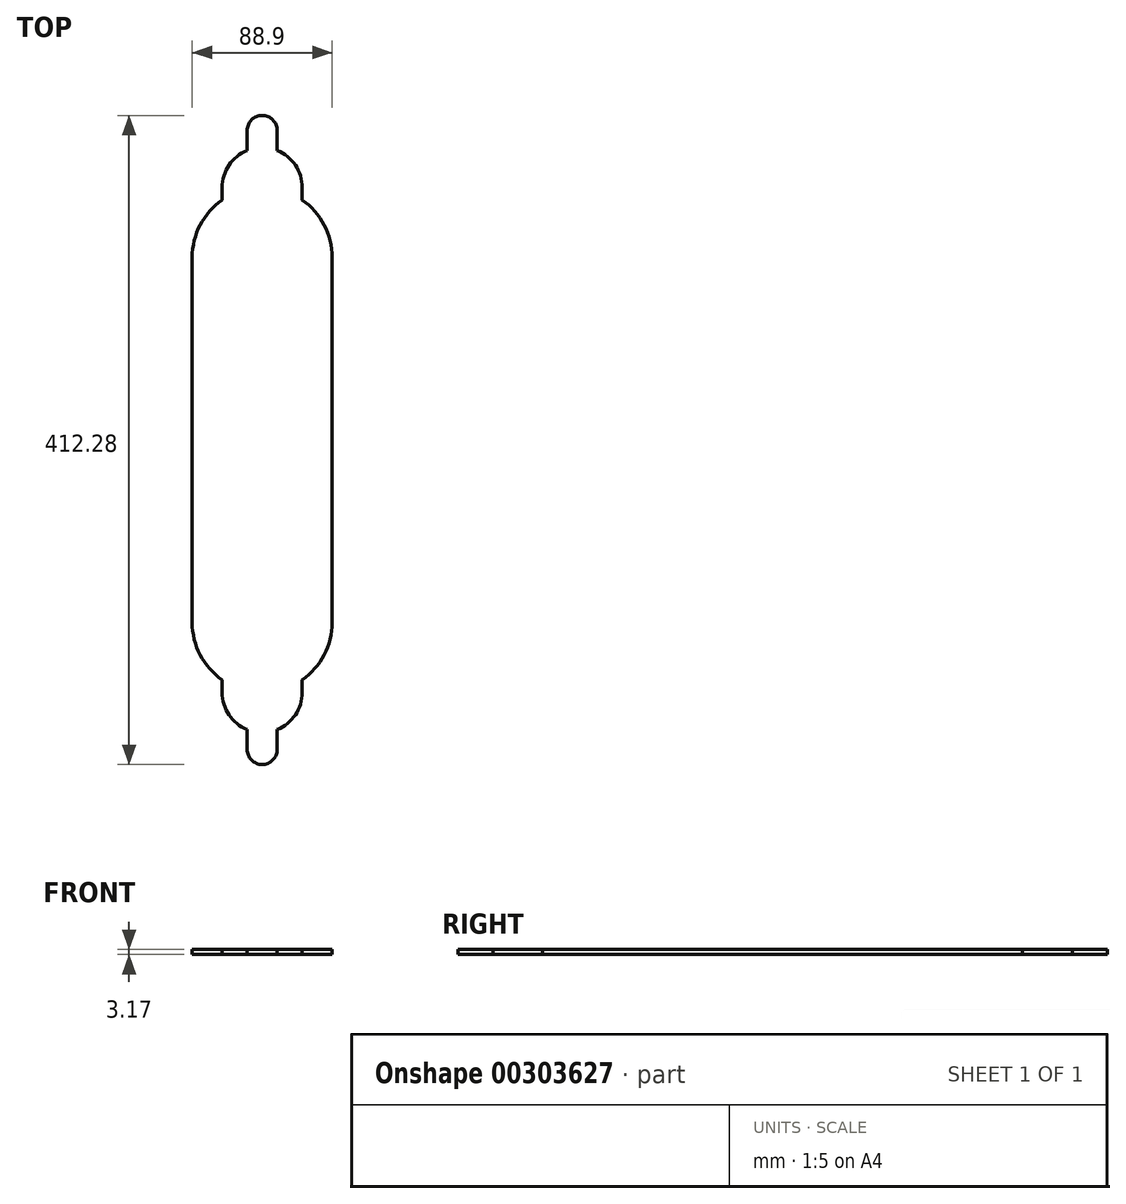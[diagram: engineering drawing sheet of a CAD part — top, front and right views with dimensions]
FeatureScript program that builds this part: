
annotation { "Feature Type Name" : "Feature", "Feature Type Description" : "" }
export const myFeature = defineFeature(function(context is Context, id is Id, definition is map)
    precondition{}
    {
        {
            var Q0;
            Q0=qCreatedBy(makeId("Top.planeOp"),FACE);
            var sketch = newSketch(context, id + "F0", { "sketchPlane" : qUnion([Q0])});
            skLineSegment(sketch, "E0.top", {"start": v(0, 263.5) * mm, "end": v(88.9, 263.5) * mm, "construction": true});
            skLineSegment(sketch, "E0.left", {"start": v(0, 147.59) * mm, "end": v(0, 263.5) * mm});
            skLineSegment(sketch, "E0.right", {"start": v(88.9, 147.59) * mm, "end": v(88.9, 263.5) * mm});
            skArc(sketch, "E1", {"start": v(69.85, 111.1) * mm, "mid": v(83.85, 127.01) * mm, "end": v(88.9, 147.59) * mm});
            skArc(sketch, "E2", {"start": v(53.98, 79.6) * mm, "mid": v(65.51, 88.94) * mm, "end": v(69.85, 103.14) * mm});
            skLineSegment(sketch, "E3", {"start": v(44.45, 147.59) * mm, "end": v(44.45, 66.9) * mm, "construction": true});
            skArc(sketch, "E4", {"start": v(34.93, 66.9) * mm, "mid": v(44.45, 57.37) * mm, "end": v(53.98, 66.9) * mm});
            skLineSegment(sketch, "E5", {"start": v(34.93, 66.9) * mm, "end": v(34.93, 79.6) * mm});
            skLineSegment(sketch, "E6", {"start": v(53.98, 66.9) * mm, "end": v(53.98, 79.6) * mm});
            skLineSegment(sketch, "E7", {"start": v(69.85, 103.14) * mm, "end": v(69.85, 111.1) * mm});
            skLineSegment(sketch, "E8", {"start": v(19.05, 103.14) * mm, "end": v(19.05, 111.1) * mm});
            skArc(sketch, "E9.trimOffspring", {"start": v(19.05, 103.14) * mm, "mid": v(23.39, 88.94) * mm, "end": v(34.92, 79.6) * mm});
            skArc(sketch, "E10.trimOffspring", {"start": v(0, 147.59) * mm, "mid": v(5.05, 127.01) * mm, "end": v(19.05, 111.1) * mm});
            skLineSegment(sketch, "E11.MirrorCS", {"start": v(69.85, 423.88) * mm, "end": v(69.85, 415.9) * mm});
            skLineSegment(sketch, "E12.MirrorCS", {"start": v(34.93, 460.13) * mm, "end": v(34.93, 447.43) * mm});
            skLineSegment(sketch, "E13.MirrorCS", {"start": v(19.05, 423.88) * mm, "end": v(19.05, 415.9) * mm});
            skLineSegment(sketch, "E14.MirrorCS", {"start": v(53.98, 460.13) * mm, "end": v(53.98, 447.43) * mm});
            skLineSegment(sketch, "E15.MirrorCS", {"start": v(44.45, 379.43) * mm, "end": v(44.45, 460.13) * mm, "construction": true});
            skArc(sketch, "E16.MirrorCS", {"start": v(34.93, 460.13) * mm, "mid": v(44.45, 469.65) * mm, "end": v(53.98, 460.13) * mm});
            skArc(sketch, "E17.MirrorCS", {"start": v(69.85, 415.9) * mm, "mid": v(83.85, 400) * mm, "end": v(88.9, 379.43) * mm});
            skArc(sketch, "E18.MirrorCS", {"start": v(19.05, 423.88) * mm, "mid": v(23.39, 438.08) * mm, "end": v(34.93, 447.43) * mm});
            skArc(sketch, "E19.MirrorCS", {"start": v(0, 379.43) * mm, "mid": v(5.05, 400) * mm, "end": v(19.05, 415.9) * mm});
            skArc(sketch, "E20.MirrorCS", {"start": v(53.98, 447.43) * mm, "mid": v(65.51, 438.08) * mm, "end": v(69.85, 423.88) * mm});
            skLineSegment(sketch, "E21.MirrorCS", {"start": v(0, 379.43) * mm, "end": v(0, 263.5) * mm});
            skLineSegment(sketch, "E22.MirrorCS", {"start": v(88.9, 379.43) * mm, "end": v(88.9, 263.5) * mm});
            skSolve(sketch);
        }
        {
            var Q0;
            Q0=makeQuery(id+"F0.imprint","IMPRINT",FACE,{"disambiguationData":[TD([[makeQuery(id+"F0.imprint","IMPRINT",EDGE,{"derivedFrom":sQuery(id+"F0.wireOp",EDGE,"E0.left")}),-1.0]])]});
            extrude(context, id + "F1", {"entities" : qUnion([Q0]), "depth" : 3.17 * mm});
        }
    });
